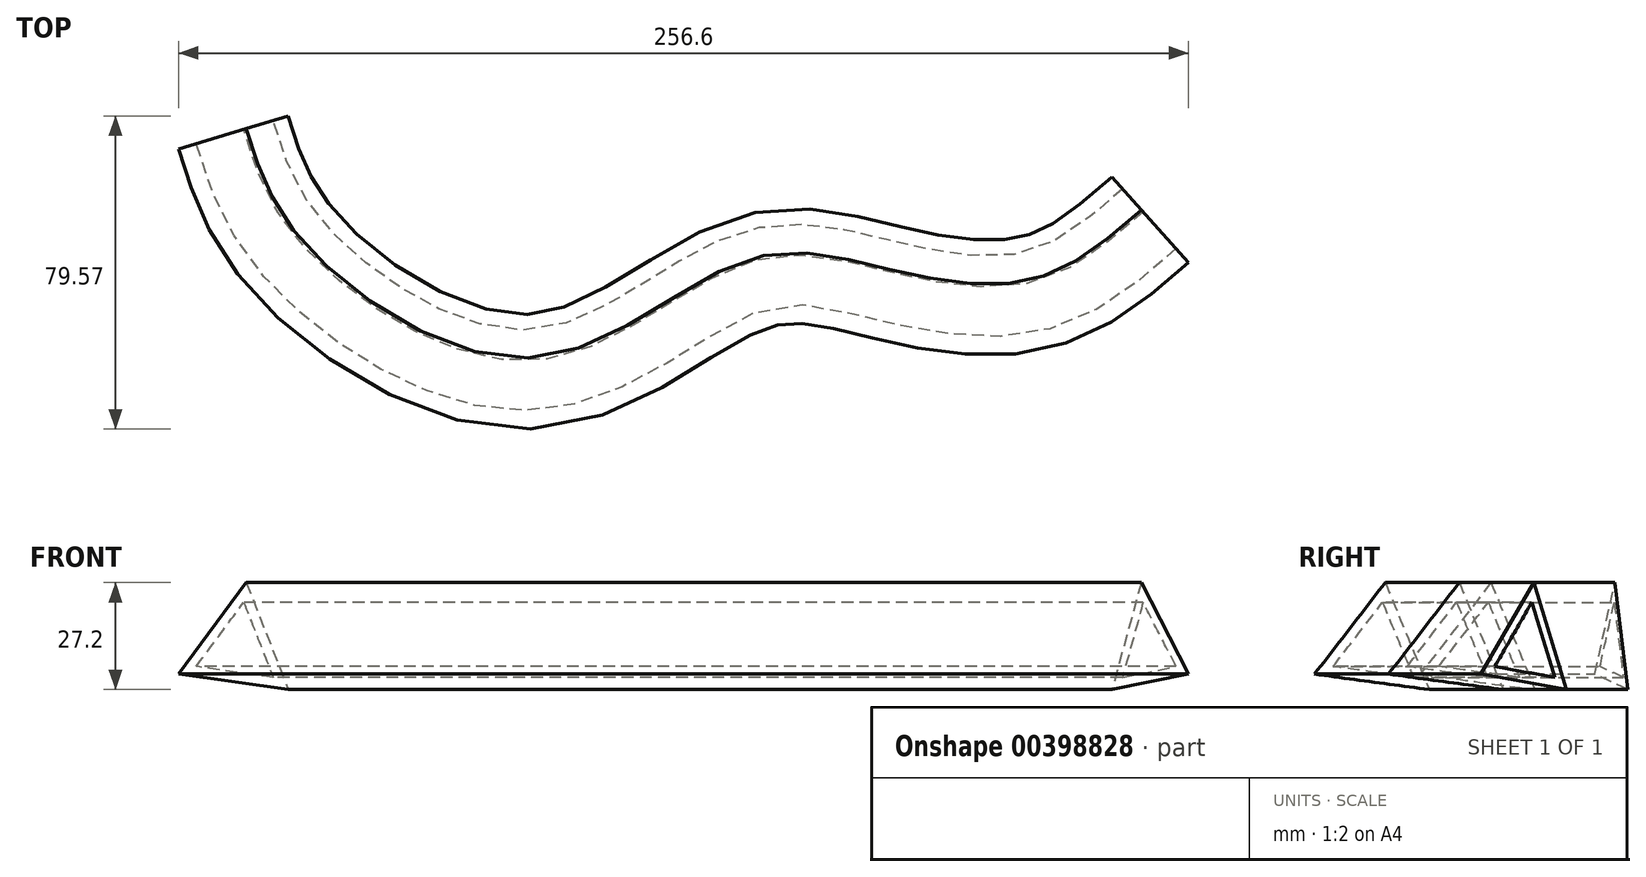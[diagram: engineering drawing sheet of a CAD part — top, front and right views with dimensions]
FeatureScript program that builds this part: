
annotation { "Feature Type Name" : "Feature", "Feature Type Description" : "" }
export const myFeature = defineFeature(function(context is Context, id is Id, definition is map)
    precondition{}
    {
        {
            var Q0;
            Q0=qCreatedBy(makeId("Top.planeOp"),FACE);
            var sketch = newSketch(context, id + "F0", { "sketchPlane" : qUnion([Q0])});
            skFitSpline(sketch, "E0", {"points": [v(-114.94, 55.6) * mm, v(-99.73, 25.6) * mm, v(-39.13, -4.26) * mm, v(15.17, 20.74) * mm, v(51.37, 17.97) * mm, v(86.64, 15.5) * mm, v(116.13, 33.91) * mm], "startDerivative": vector(63.43, -211.1) * mm, "endDerivative": vector(208.4, 186.91) * mm});
            skSolve(sketch);
        }
        {
            var Q0;
            Q0=sQuery(id+"F0.wireOp",EDGE,"E0");
            var Q1;
            Q1=sQuery(id+"F0.wireOp",VERTEX,"E0.6.internal");
            cPlane(context, id + "F1", {"entities" : qUnion([Q0, Q1]), "cplaneType" : CPlaneType.CURVE_POINT, "offset" : 25.4 * mm, "width" : 152.4 * mm, "height" : 152.4 * mm});
        }
        {
            var Q0;
            Q0=qCreatedBy(id+"F1.planeOp",FACE);
            var sketch = newSketch(context, id + "F2", { "sketchPlane" : qUnion([Q0])});
            skCircle(sketch, "E1.cCircle", {"center": v(-52.3, 0) * mm, "radius": 8.49 * mm, "construction": true});
            skLineSegment(sketch, "E1.0", {"start": v(-68, -6.44) * mm, "end": v(-50.02, 16.82) * mm});
            skLineSegment(sketch, "E1.1", {"start": v(-50.02, 16.82) * mm, "end": v(-38.86, -10.38) * mm});
            skLineSegment(sketch, "E1.2", {"start": v(-38.86, -10.38) * mm, "end": v(-68, -6.44) * mm});
            skPoint(sketch, "E1.0.midPoint", {"position": v(-59, 5.19) * mm});
            skSolve(sketch);
        }
        {
            var Q0;
            Q0=makeQuery(id+"F2.imprint","IMPRINT",FACE,{"disambiguationData":[TD([[makeQuery(id+"F2.imprint","IMPRINT",EDGE,{"derivedFrom":sQuery(id+"F2.wireOp",EDGE,"E1.0")}),-1.0]])]});
            var Q1;
            Q1=sQuery(id+"F0.wireOp",EDGE,"E0");
            sweep(context, id + "F3", {"profiles" : qUnion([Q0]), "path" : qUnion([Q1])});
        }
        {
            var Q0;
            Q0=makeQuery(id+"F3.opSweep","CAP_FACE",FACE,{"disambiguationData":[OSD([sQuery(id+"F0.wireOp",VERTEX,"E0.start"),sQuery(id+"F2.wireOp",EDGE,"E1.0"),sQuery(id+"F2.wireOp",EDGE,"E1.1"),sQuery(id+"F2.wireOp",EDGE,"E1.2")])],"isStart":false});
            var Q1;
            Q1=makeQuery(id+"F3.opSweep","CAP_FACE",FACE,{"disambiguationData":[OSD([sQuery(id+"F0.wireOp",VERTEX,"E0.end"),sQuery(id+"F2.wireOp",EDGE,"E1.0"),sQuery(id+"F2.wireOp",EDGE,"E1.1"),sQuery(id+"F2.wireOp",EDGE,"E1.2")])],"isStart":true});
            shell(context, id + "F4", {"entities" : qUnion([Q0, Q1]), "thickness" : 2.54 * mm});
        }
    });
